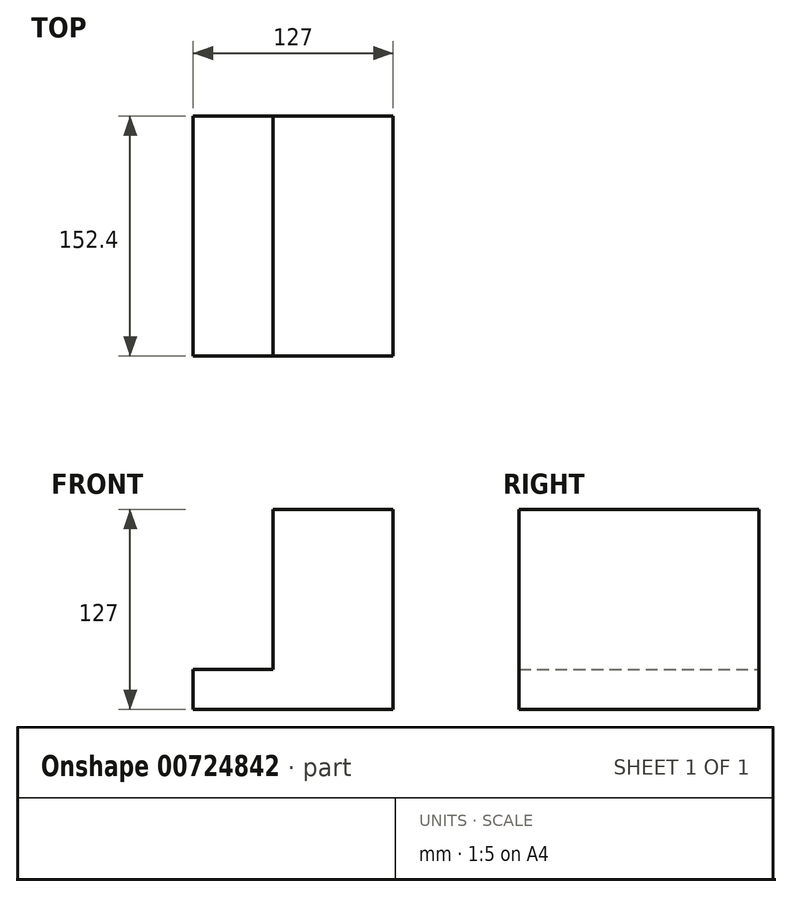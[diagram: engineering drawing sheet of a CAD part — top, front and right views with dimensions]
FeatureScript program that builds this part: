
annotation { "Feature Type Name" : "Feature", "Feature Type Description" : "" }
export const myFeature = defineFeature(function(context is Context, id is Id, definition is map)
    precondition{}
    {
        {
            var Q0;
            Q0=qCreatedBy(makeId("Front.planeOp"),FACE);
            var sketch = newSketch(context, id + "F0", { "sketchPlane" : qUnion([Q0])});
            skLineSegment(sketch, "E0", {"start": v(-127, -76.23) * mm, "end": v(0, -76.23) * mm});
            skLineSegment(sketch, "E1", {"start": v(0, -76.23) * mm, "end": v(0, 50.77) * mm});
            skLineSegment(sketch, "E2", {"start": v(0, 50.77) * mm, "end": v(-76.2, 50.77) * mm});
            skLineSegment(sketch, "E3", {"start": v(-76.2, 50.77) * mm, "end": v(-76.2, -50.83) * mm});
            skLineSegment(sketch, "E4", {"start": v(-76.2, -50.83) * mm, "end": v(-127, -50.83) * mm});
            skLineSegment(sketch, "E5", {"start": v(-127, -50.83) * mm, "end": v(-127, -76.23) * mm});
            skSolve(sketch);
        }
        {
            var Q0;
            Q0 = qSketchRegion(id + "F0", true);
            extrude(context, id + "F1", {"entities" : qUnion([Q0]), "depth" : 152.4 * mm, "offsetDistance" : 25.4 * mm});
        }
    });
